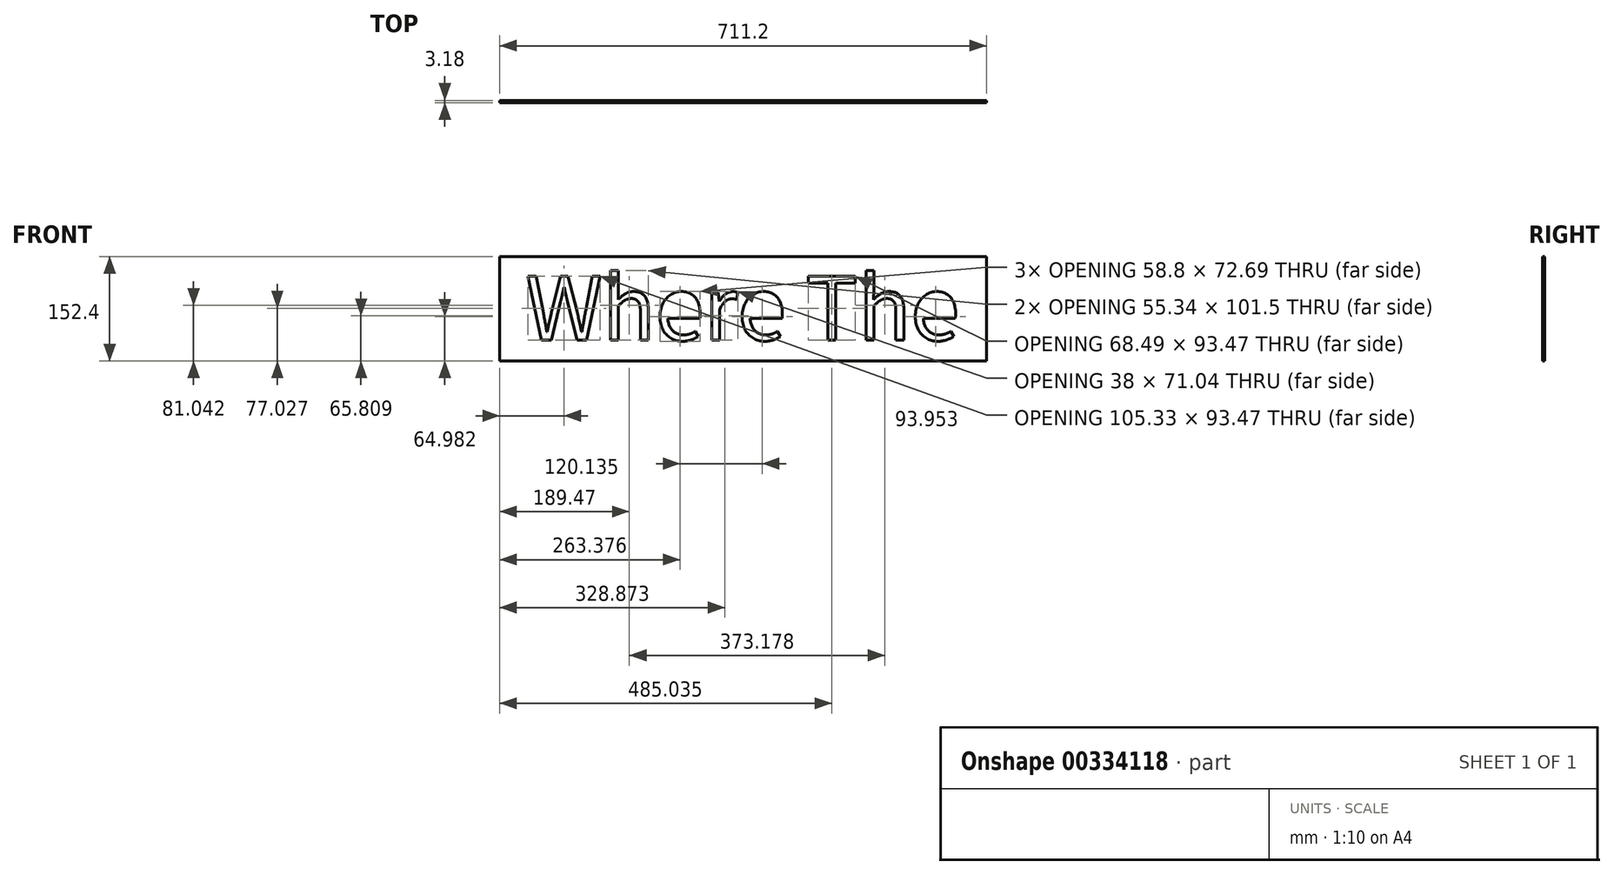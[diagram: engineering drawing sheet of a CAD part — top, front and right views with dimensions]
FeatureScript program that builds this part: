
annotation { "Feature Type Name" : "Feature", "Feature Type Description" : "" }
export const myFeature = defineFeature(function(context is Context, id is Id, definition is map)
    precondition{}
    {
        {
            var Q0;
            Q0=qCreatedBy(makeId("Front.planeOp"),FACE);
            var sketch = newSketch(context, id + "F0", { "sketchPlane" : qUnion([Q0])});
            skLineSegment(sketch, "E0.bottom", {"start": v(-355.6, 76.2) * mm, "end": v(355.6, 76.2) * mm});
            skLineSegment(sketch, "E0.top", {"start": v(-355.6, -76.2) * mm, "end": v(355.6, -76.2) * mm});
            skLineSegment(sketch, "E0.left", {"start": v(-355.6, 76.2) * mm, "end": v(-355.6, -76.2) * mm});
            skLineSegment(sketch, "E0.right", {"start": v(355.6, 76.2) * mm, "end": v(355.6, -76.2) * mm});
            skPoint(sketch, "E0.middle", {"position": v(0, 0) * mm});
            skText(sketch, "E1", { "text": "Where The", "fontName": "NotoSansCJKtc-Regular.otf"});
            const initialGuessF0  = {"E1": [-0.3175, -0.04591, 1, 0, 0.09182]};
            skSetInitialGuess(sketch, initialGuessF0);
            skSolve(sketch);
        }
        {
            var Q0;
            Q0=qSketchRegion(id+"F0",true);
            extrude(context, id + "F1", {"entities" : qUnion([Q0]), "depth" : 3.17 * mm});
        }
    });
